# Revit family: Bath&ShowerMixer-(Built-in)-Vitra-OriginSeries-A42619
name_source: partatom
category: Plumbing Fixtures
revit_build: Autodesk Revit 2017 (Build: 20160225_1515(x64)
units: mm (PartAtom-declared; Revit-internal decimal feet)

## family parameters
Cut with Voids When Loaded = No
Host = Face
OmniClass Number = 23.45.55.17
OmniClass Title = Mixing Faucets
Part Type = Normal
Room Calculation Point = No
Round Connector Dimension = Use Diameter
Shared = Yes

## types (4) — shared parameters
BIMobject category = Bath/Shower Mixer
Brand = VitrA
CW Connection = Yes
Default Elevation = 850 mm  [stored 2.78871 ft]
Description = Origin Bath/Shower Mixer
Design country = Turkey
HW Connection = Yes
Hot Water Supply (max.) = 80 °C
Hot Water temperature, factory set to = 38 °C
IFC Classification = Sanitary Terminal
Main Material = Brass
Manufacturer = VitrA
Manufacturer name = VitrA
Masterformat 2014 Code = 22 40 00
Masterformat 2014 Description = Plumbing Fixtures
Min. flow pressure of = 0.5 bar
Mounting type = Wall Mounted
NBS Referans Code = 45-35-70/315
NBS Referans Description = Water supply fittings for baths
Nominal Depth (mm) = 96 mm  [stored 0.314961 ft]
Nominal Height (mm) = 123 mm
Nominal Width (mm) = 300 mm
Number Of Connections = 2
OmniClass Code = 23.45.55.17
OmniClass Description = Mixing Faucets
Product Properties = Extra Water Saving, Green Building Certification, Energy Saving, Easy İnstallation
Product Type = Bath&Shower Mixer
Product certification = https://www.vitraglobal.com
Product data url = https://www.vitraglobal.com
Product family = Origin
Product group = Origin Bath&Shower Mixer
Range of Hot Water Supply = 5 - 65 °C
Range of flow pressure = 1 - 5 bar
Technical description = https://www.vitraglobal.com
Test Pressure = 16 bar
URL = https://vitraglobal.com
Uniclass 1.4 Code = L725111
Uniclass 1.4 Description = Mixer taps
Uniclass 2.0 Code = Pr_40_20_87_09
Uniclass 2.0 Description = Bath taps
Uniclass 2015 Code = Pr_40_20_87_09
Uniclass 2015 Name = Bath taps
Uniformat II Code = 22 40 00
Uniformat II Description = Plumbing Fixture
Vent Connection = No
Warranty Period (Year) = 10 Years
Waste Connection = No
Weight Net (kg) = 3.2
Youtube = https://www.youtube.com

## per-type parameters (varying)
| type | Article No. (default) | Coating Material | Color | Connection Diameter (mm) | Model | Product SKU |
| Bath&ShowerMixer-Vitra-OriginSeries(MatteBlack)-A4261936 | A4261936 | Matte Black | Matte Black | 15 mm  [stored 0.0492126 ft] | A4261936 | A4261936 |
| Bath&ShowerMixer-Vitra-OriginSeries(Nickel)-A4261934 | A4261934 | Nickel | Nickel | 15 mm  [stored 0.0492126 ft] | A4261934 | A4261934 |
| Bath&ShowerMixer-Vitra-OriginSeries(Bright Copper)-A4261926 | A4261926 | BrightCopper | BrightCopper | 10 mm  [stored 0.0328084 ft] | A4261926 | A4261926 |
| Bath&ShowerMixer-Vitra-OriginSeries(Chrome)-A42619 | A42619 | Chrome | Chrome | 15 mm  [stored 0.0492126 ft] | A42619 | A42619 |

note: [stored X ft] marks values corroborated as IEEE doubles in the binary element streams (Revit-internal decimal feet)

## geometry (parser evidence)
native form markers: Sweep x2
no freeform markers — native parametric forms only
